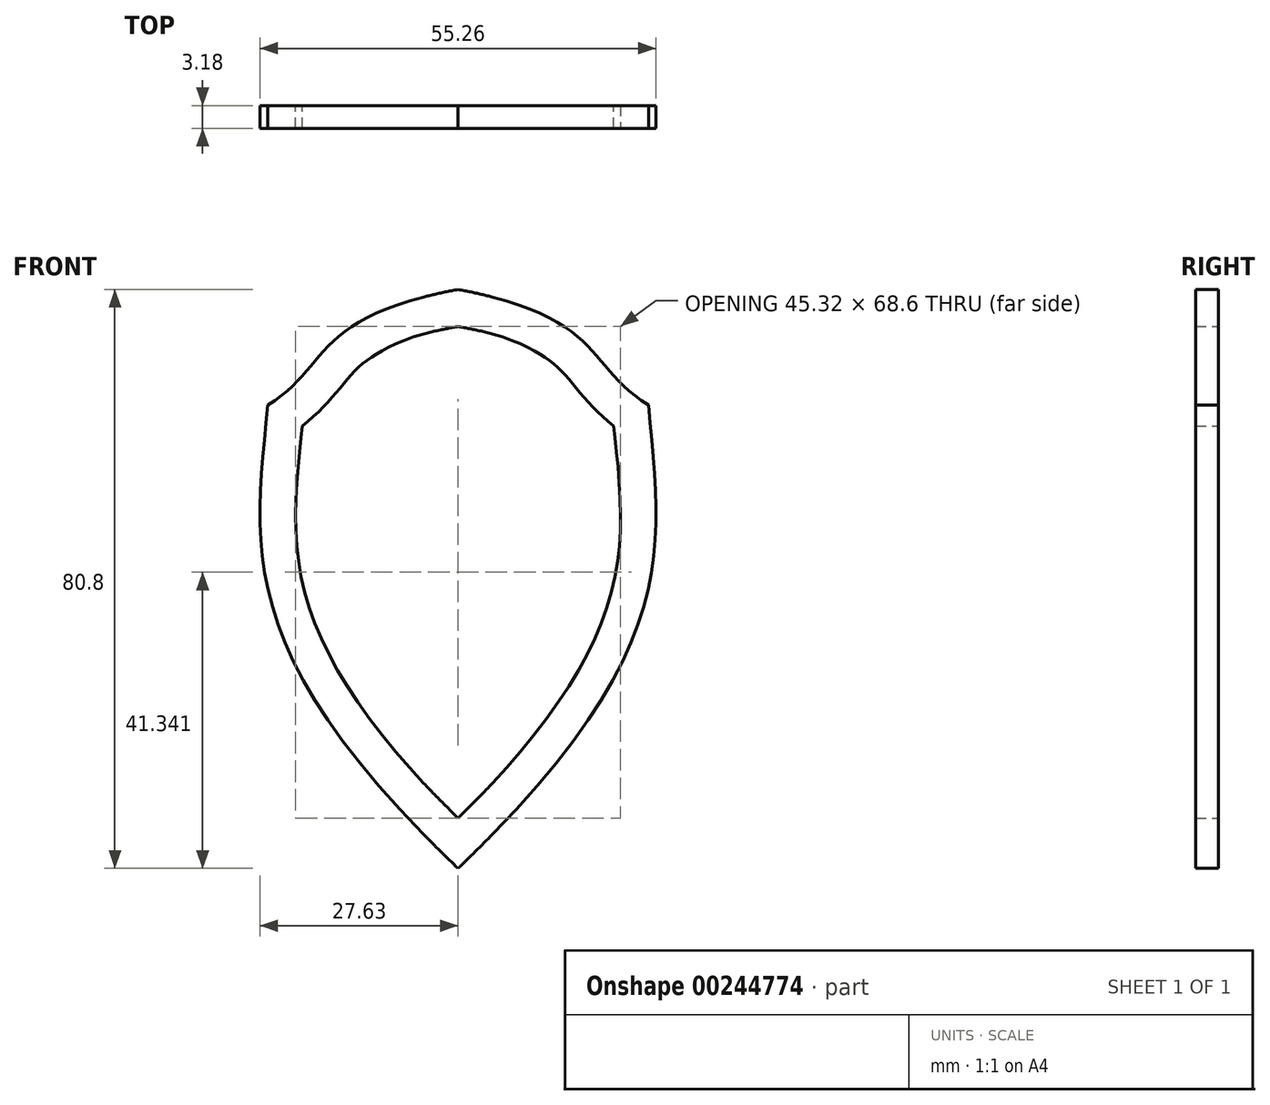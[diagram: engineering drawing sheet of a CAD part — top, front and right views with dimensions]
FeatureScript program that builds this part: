
annotation { "Feature Type Name" : "Feature", "Feature Type Description" : "" }
export const myFeature = defineFeature(function(context is Context, id is Id, definition is map)
    precondition{}
    {
        {
            var Q0;
            Q0=qCreatedBy(makeId("Front.planeOp"),FACE);
            var sketch = newSketch(context, id + "F0", { "sketchPlane" : qUnion([Q0])});
            skLineSegment(sketch, "E0", {"start": v(0, -60.63) * mm, "end": v(0, 141.04) * mm, "construction": true});
            skFitSpline(sketch, "E1", {"points": [v(0, -40.6) * mm, v(-26.56, 24.06) * mm], "startDerivative": vector(-94.3, 90.63) * mm, "endDerivative": vector(5.61, 60.71) * mm});
            skFitSpline(sketch, "E2", {"points": [v(-26.56, 24.06) * mm, v(0, 40.2) * mm], "startDerivative": vector(26.56, 16.14) * mm, "endDerivative": vector(61.74, 11.54) * mm});
            skFitSpline(sketch, "E3.MirrorCS", {"points": [v(0, -40.6) * mm, v(26.56, 24.06) * mm], "startDerivative": vector(94.3, 90.63) * mm, "endDerivative": vector(-5.61, 60.71) * mm});
            skFitSpline(sketch, "E4.MirrorCS", {"points": [v(26.56, 24.06) * mm, v(0, 40.2) * mm], "startDerivative": vector(-26.56, 16.14) * mm, "endDerivative": vector(-61.74, 11.54) * mm});
            skFitSpline(sketch, "E5.0", {"points": [v(23.92, 19.72) * mm, v(23.24, 20.14) * mm, v(21.97, 21) * mm, v(20.33, 22.33) * mm, v(18.93, 23.67) * mm, v(17.74, 24.96) * mm, v(16.72, 26.16) * mm, v(15.81, 27.25) * mm, v(14.97, 28.21) * mm, v(14.14, 29.08) * mm, v(13.26, 29.88) * mm, v(12.26, 30.65) * mm, v(11.04, 31.42) * mm, v(9.02, 32.46) * mm, v(5.57, 33.78) * mm, v(1.5, 34.76) * mm, v(-0.93, 35.21) * mm]});
            skFitSpline(sketch, "E5.1", {"points": [v(-3.52, -36.94) * mm, v(0.32, -33.25) * mm, v(6.9, -26.4) * mm, v(13.91, -17.5) * mm, v(18.48, -9.78) * mm, v(21.14, -3) * mm, v(22.39, 3.29) * mm, v(22.65, 9.55) * mm, v(22.24, 16.18) * mm, v(21.74, 21.03) * mm, v(21.5, 23.6) * mm]});
            skFitSpline(sketch, "E5.2", {"points": [v(3.52, -36.94) * mm, v(-0.32, -33.25) * mm, v(-6.9, -26.4) * mm, v(-13.91, -17.5) * mm, v(-18.48, -9.78) * mm, v(-21.14, -3) * mm, v(-22.39, 3.29) * mm, v(-22.65, 9.55) * mm, v(-22.24, 16.18) * mm, v(-21.74, 21.03) * mm, v(-21.5, 23.6) * mm]});
            skFitSpline(sketch, "E5.3", {"points": [v(-23.92, 19.72) * mm, v(-23.24, 20.14) * mm, v(-21.97, 21) * mm, v(-20.33, 22.33) * mm, v(-18.93, 23.67) * mm, v(-17.74, 24.96) * mm, v(-16.72, 26.16) * mm, v(-15.81, 27.25) * mm, v(-14.97, 28.21) * mm, v(-14.14, 29.08) * mm, v(-13.26, 29.88) * mm, v(-12.26, 30.65) * mm, v(-11.04, 31.42) * mm, v(-9.02, 32.46) * mm, v(-5.57, 33.78) * mm, v(-1.5, 34.76) * mm, v(0.93, 35.21) * mm]});
            skLineSegment(sketch, "E6", {"start": v(4.83, 39.14) * mm, "end": v(4.83, 33.88) * mm});
            skLineSegment(sketch, "E7.MirrorCS", {"start": v(-4.83, 39.14) * mm, "end": v(-4.83, 33.88) * mm});
            skLineSegment(sketch, "E8.trimOffspring", {"start": v(4.83, -28.41) * mm, "end": v(4.83, -35.81) * mm});
            skLineSegment(sketch, "E9.trimOffspring", {"start": v(-4.83, -28.41) * mm, "end": v(-4.83, -35.81) * mm});
            skText(sketch, "E10", { "text": "OD", "fontName": "AllertaStencil-Regular.ttf"});
            skText(sketch, "E11", { "text": "W", "fontName": "AllertaStencil-Regular.ttf"});
            skLineSegment(sketch, "E12", {"start": v(-47.58, 1.67) * mm, "end": v(92.13, 1.67) * mm, "construction": true});
            const initialGuessF0  = {"E10": [-0.01742, 0.00494, 1, 0, 0.01682], "E11": [-0.01143, -0.016, 1, 0, 0.01545]};
            skSetInitialGuess(sketch, initialGuessF0);
            skSolve(sketch);
        }
        {
            var Q0;
            Q0 = qSketchRegion(id + "F0", true);
            extrude(context, id + "F1", {"entities" : qUnion([Q0]), "depth" : 3.17 * mm});
        }
    });
